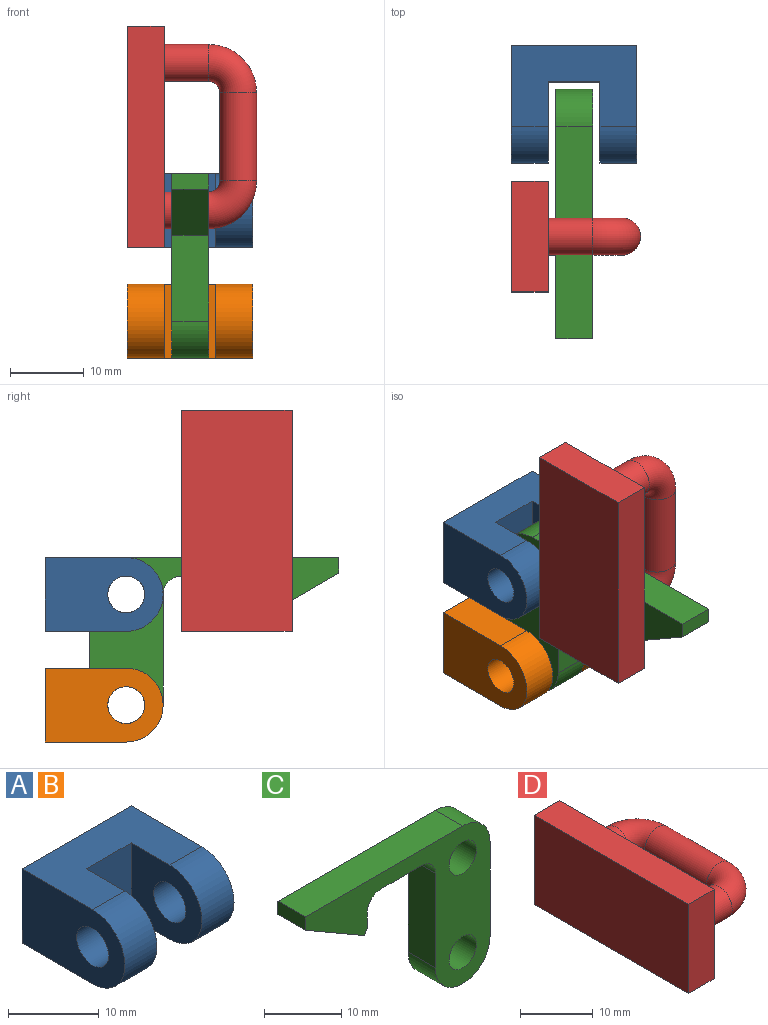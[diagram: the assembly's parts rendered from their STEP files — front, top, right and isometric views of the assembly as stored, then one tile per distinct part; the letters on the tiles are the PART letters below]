
ASSEMBLY  parts=4 mates=3
PART A: 12 faces, bbox 17x16x10 mm
  f0: cylinder r=5mm len=10mm, axis (-1,0,0), area 78.5mm2, adj f1,f4,f7,f9
  f1: plane 17x11mm, normal (0,0,-1), area 145mm2, adj f0,f3,f5,f7,f8,f9,f10,f11
  f2: cylinder r=2.5mm len=5mm, axis (-1,0,0), area 78.5mm2, adj f7,f9
  f3: plane 17x10mm, normal (0,1,0), area 170mm2, adj f1,f4,f7,f8
  f4: plane 17x11mm, normal (0,0,1), area 145mm2, adj f0,f3,f5,f7,f8,f9,f10,f11
  f5: cylinder r=5mm len=10mm, axis (-1,0,0), area 78.5mm2, adj f1,f4,f8,f10
  f6: cylinder r=2.5mm len=5mm, axis (-1,0,0), area 78.5mm2, adj f8,f10
  f7: plane 16x10mm, normal (1,0,0), area 129.6mm2, adj f0,f1,f2,f3,f4
  f8: plane 16x10mm, normal (-1,0,0), area 129.6mm2, adj f1,f3,f4,f5,f6
  f9: plane 11x10mm, normal (-1,0,0), area 79.6mm2, adj f0,f1,f2,f4,f11
  f10: plane 11x10mm, normal (1,0,0), area 79.6mm2, adj f1,f4,f5,f6,f11
  f11: plane 10x7mm, normal (0,-1,0), area 70mm2, adj f1,f4,f9,f10
PART B: same geometry as A
PART C: 16 faces, bbox 33.8x5x25 mm
  f0: cylinder r=2.5mm len=5mm, axis (0,1,0), area 19.6mm2, adj f1,f11,f13,f14
  f1: plane 15x5mm, normal (-1,0,0), area 75mm2, adj f0,f13,f14,f15
  f2: plane 15x5mm, normal (1,0,0), area 75mm2, adj f3,f13,f14,f15
  f3: cylinder r=5mm len=5mm, axis (0,1,0), area 39.3mm2, adj f2,f4,f13,f14
  f4: plane 28.83x5mm, normal (0,0,1), area 144.2mm2, adj f3,f5,f13,f14
  f5: plane 5x2.11mm, normal (-1,0,0), area 10.6mm2, adj f4,f6,f13,f14
  f6: plane 10.83x6.25mm, normal (-0.5,0,-0.87), area 62.5mm2, adj f5,f7,f13,f14
  f7: plane 5x0.87mm, normal (0.87,0,-0.5), area 5mm2, adj f6,f8,f13,f14
  f8: plane 5x2.5mm, normal (1,0,0), area 12.5mm2, adj f7,f9,f13,f14
  f9: cylinder r=2.5mm len=5mm, axis (0,1,0), area 19.6mm2, adj f8,f11,f13,f14
  f10: cylinder r=2.5mm len=5mm, axis (0,1,0), area 78.5mm2, adj f13,f14
  f11: plane 7.5x5mm, normal (0,0,-1), area 37.5mm2, adj f0,f9,f13,f14
  f12: cylinder r=2.5mm len=5mm, axis (0,1,0), area 78.5mm2, adj f13,f14
  f13: plane 33.83x25mm, normal (0,-1,0), area 289.3mm2, adj f0,f1,f2,f3,f4,f5,f6,f7
  f14: plane 33.83x25mm, normal (0,1,0), area 289.3mm2, adj f0,f1,f2,f3,f4,f5,f6,f7
  f15: cylinder r=5mm len=10mm, axis (0,1,0), area 78.5mm2, adj f1,f2,f13,f14
PART D: 11 faces, bbox 18x30x15 mm
  f0: cylinder r=2.5mm len=6mm, axis (1,0,0), area 94.2mm2, adj f1,f5
  f1: torus R=4mm, axis (0,0,-1), area 98.7mm2, adj f0,f2
  f2: cylinder r=2.5mm len=12mm, axis (0,-1,0), area 188.5mm2, adj f1,f3
  f3: torus R=4mm, axis (0,0,-1), area 98.7mm2, adj f2,f4
  f4: cylinder r=2.5mm len=6mm, axis (-1,0,0), area 94.2mm2, adj f3,f5
  f5: plane 30x15mm, normal (1,0,0), area 410.7mm2, adj f0,f4,f6,f7,f8,f9
  f6: plane 30x5mm, normal (0,0,1), area 150mm2, adj f5,f7,f9,f10
  f7: plane 15x5mm, normal (0,-1,0), area 75mm2, adj f5,f6,f8,f10
  f8: plane 30x5mm, normal (0,0,-1), area 150mm2, adj f5,f7,f9,f10
  f9: plane 15x5mm, normal (0,1,0), area 75mm2, adj f5,f6,f8,f10
  f10: plane 30x15mm, normal (-1,0,0), area 450mm2, adj f6,f7,f8,f9
PLACE A t=(6.73,19.72,13.25)mm fixed
PLACE B t=(6.73,19.72,-1.75)mm
PLACE C rot(axis=(0,0,1),90deg) t=(4.23,19.72,13.25)mm
PLACE D rot(axis=(-1,0,0),90deg) t=(3.23,4.74,23.25)mm
MATE fastened B.f3 <-> A.f3  axis (0,1,0) through (6.73,30.72,3.25)mm
MATE slider D.f8 <-> A.f3  axis (0,-1,0) through (-1.77,-2.76,23.25)mm
MATE revolute C.f12 <-> A.f0  axis (-1,0,0) through (4.23,19.72,13.25)mm
